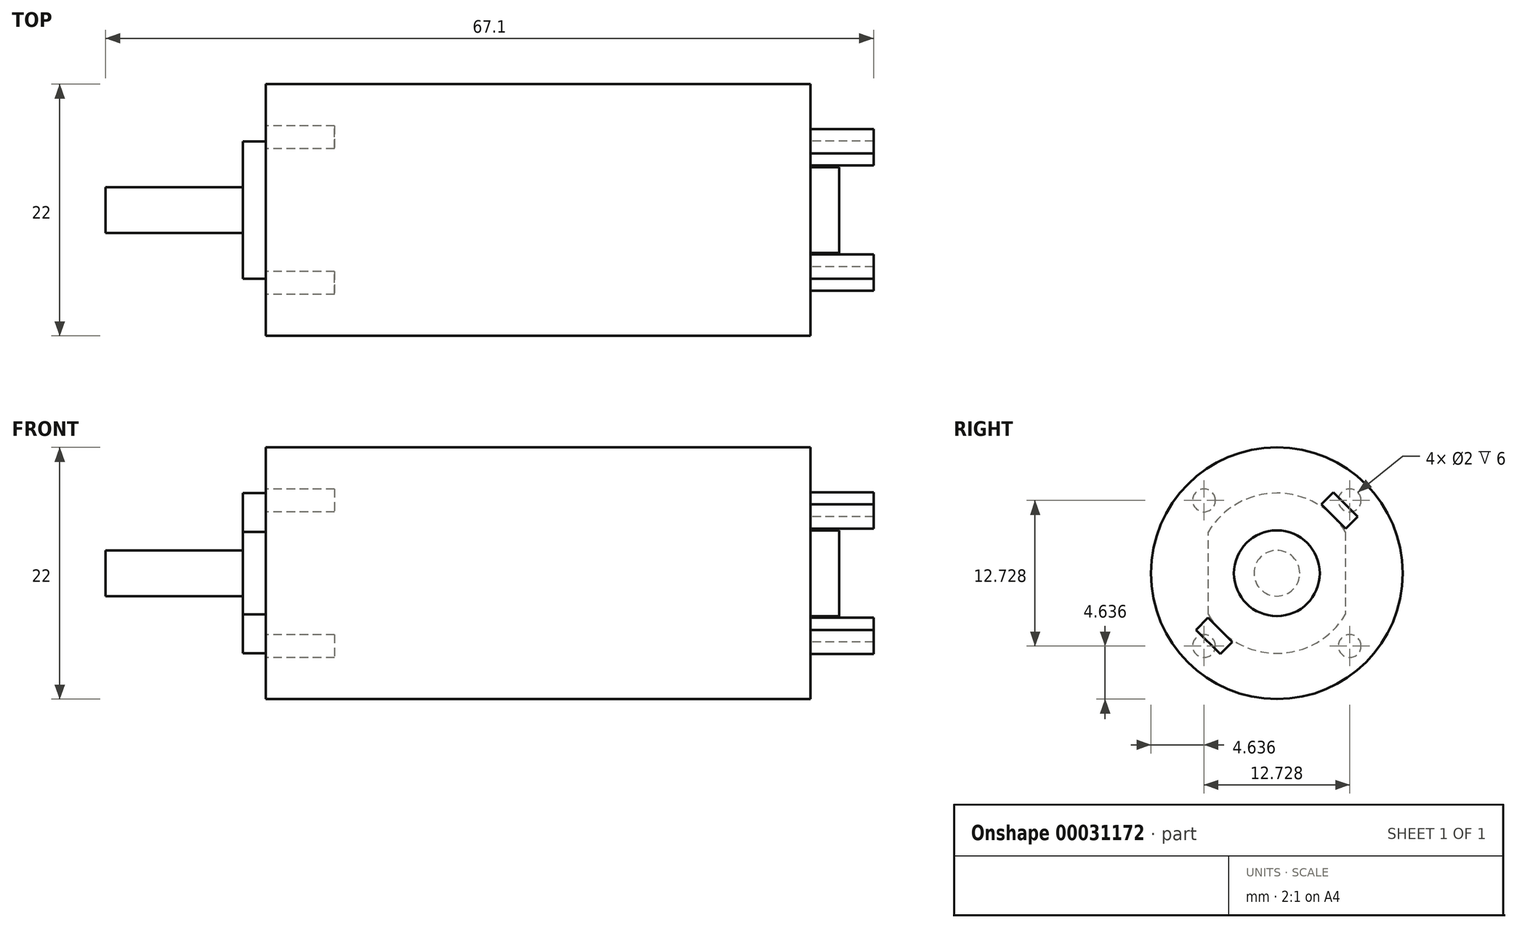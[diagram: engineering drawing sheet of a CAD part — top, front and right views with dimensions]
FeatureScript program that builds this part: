
annotation { "Feature Type Name" : "Feature", "Feature Type Description" : "" }
export const myFeature = defineFeature(function(context is Context, id is Id, definition is map)
    precondition{}
    {
        {
            var Q0;
            Q0=qCreatedBy(makeId("Right.planeOp"),FACE);
            var sketch = newSketch(context, id + "F0", { "sketchPlane" : qUnion([Q0])});
            skCircle(sketch, "E0", {"center": v(0, 0) * mm, "radius": 11 * mm});
            skSolve(sketch);
        }
        {
            var Q0;
            Q0 = qSketchRegion(id + "F0", true);
            extrude(context, id + "F1", {"entities" : qUnion([Q0]), "offsetDistance" : 25 * mm, "depth" : 47.6 * mm});
        }
        {
            var Q0;
            Q0=makeQuery(id+"F1.opExtrude","CAP_FACE",FACE,{"disambiguationData":[OSD([sQuery(id+"F0.wireOp",EDGE,"E0")])],"isStart":true});
            var sketch = newSketch(context, id + "F2", { "sketchPlane" : qUnion([Q0])});
            skArc(sketch, "E1", {"start": v(-6, -3.6) * mm, "mid": v(0, -7) * mm, "end": v(6, -3.6) * mm});
            skLineSegment(sketch, "E2", {"start": v(-6, 3.6) * mm, "end": v(-6, -3.6) * mm});
            skLineSegment(sketch, "E3", {"start": v(6, -3.6) * mm, "end": v(6, 3.6) * mm});
            skArc(sketch, "E4.trimOffspring", {"start": v(6, 3.6) * mm, "mid": v(0, 7) * mm, "end": v(-6, 3.6) * mm});
            skSolve(sketch);
        }
        {
            var Q0;
            Q0 = qSketchRegion(id + "F2", true);
            extrude(context, id + "F3", {"entities" : qUnion([Q0]), "operationType" : NewBodyOperationType.ADD, "depth" : 2 * mm});
        }
        {
            var Q0;
            Q0=makeQuery(id+"F3.opExtrude","CAP_FACE",FACE,{"disambiguationData":[OSD([sQuery(id+"F2.wireOp",EDGE,"E1"),sQuery(id+"F2.wireOp",EDGE,"E2"),sQuery(id+"F2.wireOp",EDGE,"E3"),sQuery(id+"F2.wireOp",EDGE,"E4.trimOffspring")])],"isStart":false});
            var sketch = newSketch(context, id + "F4", { "sketchPlane" : qUnion([Q0])});
            skCircle(sketch, "E5", {"center": v(0, 0) * mm, "radius": 2 * mm});
            skSolve(sketch);
        }
        {
            var Q0;
            Q0 = qSketchRegion(id + "F4", true);
            extrude(context, id + "F5", {"entities" : qUnion([Q0]), "operationType" : NewBodyOperationType.ADD, "depth" : 12 * mm});
        }
        {
            var Q0;
            Q0=makeQuery(id+"F1.opExtrude","CAP_FACE",FACE,{"disambiguationData":[OSD([sQuery(id+"F0.wireOp",EDGE,"E0")])],"isStart":true});
            var sketch = newSketch(context, id + "F6", { "sketchPlane" : qUnion([Q0])});
            skCircle(sketch, "E6", {"center": v(6.36, 6.36) * mm, "radius": 1 * mm});
            skCircle(sketch, "E7", {"center": v(6.36, -6.36) * mm, "radius": 1 * mm});
            skCircle(sketch, "E8", {"center": v(-6.36, -6.36) * mm, "radius": 1 * mm});
            skCircle(sketch, "E9", {"center": v(-6.36, 6.36) * mm, "radius": 1 * mm});
            skLineSegment(sketch, "E10", {"start": v(-6.36, 6.36) * mm, "end": v(-6.36, -6.36) * mm, "construction": true});
            skLineSegment(sketch, "E11", {"start": v(-6.36, -6.36) * mm, "end": v(6.36, -6.36) * mm, "construction": true});
            skLineSegment(sketch, "E12", {"start": v(6.36, -6.36) * mm, "end": v(6.36, 6.36) * mm, "construction": true});
            skLineSegment(sketch, "E13", {"start": v(-6.36, 6.36) * mm, "end": v(0, 0) * mm, "construction": true});
            skLineSegment(sketch, "E14", {"start": v(6.36, -6.36) * mm, "end": v(0, 0) * mm, "construction": true});
            skSolve(sketch);
        }
        {
            var Q0;
            Q0 = qSketchRegion(id + "F6", true);
            extrude(context, id + "F7", {"entities" : qUnion([Q0]), "operationType" : NewBodyOperationType.REMOVE, "oppositeDirection" : true, "depth" : 6 * mm});
        }
        {
            var Q0;
            Q0=makeQuery(id+"F1.opExtrude","CAP_FACE",FACE,{"disambiguationData":[OSD([sQuery(id+"F0.wireOp",EDGE,"E0")])],"isStart":false});
            var sketch = newSketch(context, id + "F8", { "sketchPlane" : qUnion([Q0])});
            skCircle(sketch, "E15", {"center": v(0, 0) * mm, "radius": 3.75 * mm});
            skSolve(sketch);
        }
        {
            var Q0;
            Q0 = qSketchRegion(id + "F8", true);
            extrude(context, id + "F9", {"entities" : qUnion([Q0]), "operationType" : NewBodyOperationType.ADD, "depth" : 2.5 * mm, "offsetDistance" : 25 * mm});
        }
        {
            var Q0;
            Q0=makeQuery(id+"F1.opExtrude","CAP_FACE",FACE,{"disambiguationData":[OSD([sQuery(id+"F0.wireOp",EDGE,"E0")])],"isStart":false});
            var sketch = newSketch(context, id + "F10", { "sketchPlane" : qUnion([Q0])});
            skLineSegment(sketch, "E16", {"start": v(-6.01, -3.89) * mm, "end": v(-3.89, -6.01) * mm});
            skLineSegment(sketch, "E17", {"start": v(-3.89, -6.01) * mm, "end": v(-4.95, -7.07) * mm});
            skLineSegment(sketch, "E18", {"start": v(-4.95, -7.07) * mm, "end": v(-7.07, -4.95) * mm});
            skLineSegment(sketch, "E19", {"start": v(-7.07, -4.95) * mm, "end": v(-6.01, -3.89) * mm});
            skLineSegment(sketch, "E20", {"start": v(3.89, 6.01) * mm, "end": v(6.01, 3.89) * mm});
            skLineSegment(sketch, "E21", {"start": v(6.01, 3.89) * mm, "end": v(7.07, 4.95) * mm});
            skLineSegment(sketch, "E22", {"start": v(7.07, 4.95) * mm, "end": v(4.95, 7.07) * mm});
            skLineSegment(sketch, "E23", {"start": v(4.95, 7.07) * mm, "end": v(3.89, 6.01) * mm});
            skLineSegment(sketch, "E24", {"start": v(0, 0) * mm, "end": v(0, -14.7) * mm, "construction": true});
            skLineSegment(sketch, "E25", {"start": v(-6.01, -3.89) * mm, "end": v(0, 0) * mm, "construction": true});
            skLineSegment(sketch, "E26", {"start": v(6.01, 3.89) * mm, "end": v(0, 0) * mm, "construction": true});
            skLineSegment(sketch, "E27", {"start": v(-3.89, -6.01) * mm, "end": v(0, 0) * mm, "construction": true});
            skSolve(sketch);
        }
        {
            var Q0;
            Q0 = qSketchRegion(id + "F10", true);
            extrude(context, id + "F11", {"entities" : qUnion([Q0]), "operationType" : NewBodyOperationType.ADD, "depth" : 5.5 * mm, "offsetDistance" : 25 * mm});
        }
    });
